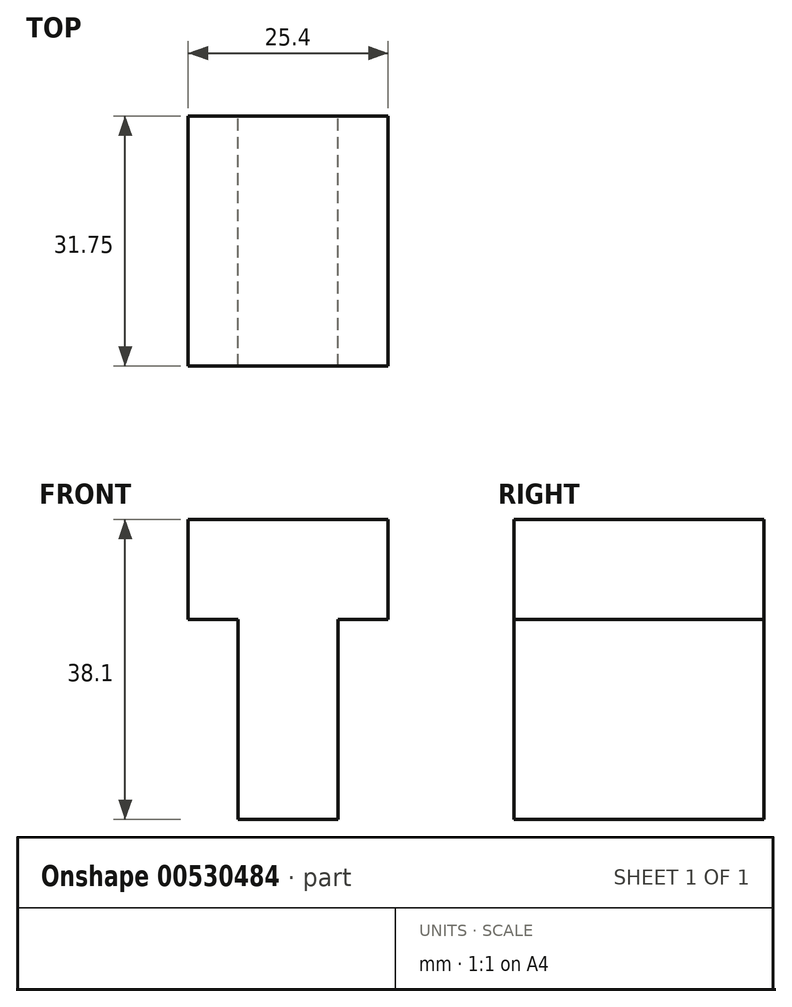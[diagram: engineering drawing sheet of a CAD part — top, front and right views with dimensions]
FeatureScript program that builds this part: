
annotation { "Feature Type Name" : "Feature", "Feature Type Description" : "" }
export const myFeature = defineFeature(function(context is Context, id is Id, definition is map)
    precondition{}
    {
        {
            var Q0;
            Q0=qCreatedBy(makeId("Front.planeOp"),FACE);
            var sketch = newSketch(context, id + "F0", { "sketchPlane" : qUnion([Q0])});
            skLineSegment(sketch, "E0", {"start": v(-35.75, 25.4) * mm, "end": v(-35.75, 0) * mm});
            skLineSegment(sketch, "E1", {"start": v(-35.75, 0) * mm, "end": v(-23.05, 0) * mm});
            skLineSegment(sketch, "E2", {"start": v(-23.05, 0) * mm, "end": v(-23.05, 25.4) * mm});
            skLineSegment(sketch, "E3", {"start": v(-23.05, 25.4) * mm, "end": v(-16.7, 25.4) * mm});
            skLineSegment(sketch, "E4", {"start": v(-16.7, 25.4) * mm, "end": v(-16.7, 38.1) * mm});
            skLineSegment(sketch, "E5", {"start": v(-16.7, 38.1) * mm, "end": v(-42.1, 38.1) * mm});
            skLineSegment(sketch, "E6", {"start": v(-42.1, 38.1) * mm, "end": v(-42.1, 25.4) * mm});
            skLineSegment(sketch, "E7", {"start": v(-42.1, 25.4) * mm, "end": v(-35.75, 25.4) * mm});
            skSolve(sketch);
        }
        {
            var Q0;
            Q0 = qSketchRegion(id + "F0", true);
            extrude(context, id + "F1", {"entities" : qUnion([Q0]), "depth" : 31.75 * mm, "offsetDistance" : 25.4 * mm});
        }
    });
